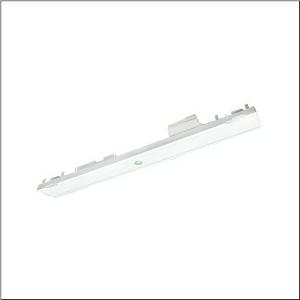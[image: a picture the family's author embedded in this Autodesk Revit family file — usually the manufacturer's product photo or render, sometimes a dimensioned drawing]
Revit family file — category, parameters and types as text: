
# Revit family: licross_r_56tl117c4x31_6d2f
name_source: partatom
category: Lighting Fixtures
units: mm (PartAtom-declared; Revit-internal decimal feet)

## family parameters
Cut with Voids When Loaded = No
Host = Face
Light Source = No
Part Type = Normal
Room Calculation Point = No
Round Connector Dimension = Use Diameter
Shared = No

## types (1)
- Licross® (1 x LED, 310 lm, 3.9 W, 4000K)
    Apparent Load = 4 VA
    CIE Flux Codes = 84 95 98 100 100
    Color Rendering = 70
    Color Temperature = 4000K
    Default Elevation = 1800 mm
    Description = Licross®, luminaire insert, of sheet steel, coil coated, white, length: 500mm, width: 59mm, height: 60mm, mounting height: 7..17m, emergency light element,LED rated luminous flux: 310lm, light colour: 740, control gear: CEAG, with plug, 6-pole, with phase selection, mains connection: 220..240V, AC/DC, 0/50..60Hz, rated input power: 3.9W, internal wiring halogen-free, for trunking rail, 9..14-core, for emergency light function, supply monitoring module CEAG, with address switch, choice between two emergency light lines via tool-free moving of contact pin prior to installation in trunking rail, primary light control with lens, of PMMA, primary optical cover: cover, of PMMA, light emission: direct distribution, primary light characteristic: symmetric,  for area, compatible with all CEAG STAR technology systems (ZB-S, DG-S (DualGuard-S), LP-STAR, AT-S+), protection rating (complete): IP40, insulation class (complete): insulation class I (protective earthing), certification: CE, UKCA, protection symbol: D if used in an environment without relevant dust loads, impact resistance: IK06, permissible ambient temperature for indoor applications: -20..+40°C, packaging unit: 1 piece
    Height = 60 mm  [stored 0.19685 ft]
    Lamp = 1 x LED
    Lamp Light Flux = 310 lm
    Lamp Power = 3.9 W
    Lamp count = 1
    Length = 500 mm  [stored 1.64042 ft]
    Luminous efficacy = 79 lm/W
    Manufacturer = Siteco
    ModVariant = No
    Model = 56TL117C4X31
    Mounting Place = Ceiling
    Mounting Type = Pendant
    Number of Poles = 1
    OnlyDefault = Yes
    Power Factor = 1
    Product Name = Licross®
    Product group = luminaire insert | ceiling pendant
    ProductGroupID = 902
    Protection Class = Protection class I
    Protection Degree = IP 40
    RLX_Detail_Level = 1
    RLX_Emergency_Light_Flux = 0 lm
    RLX_Emergency_Type = 0
    RLX_Emergency_Type_DB = No
    RlxData = <blob elided: 17853 chars, md5=111cdbb5>
    Socket = socket
    Standby Power = 0 W
    System Light Flux = 310 lm
    System Power = 4 W
    Type Comments = Product without accessories
    Type Image = l_1251804.jpg
    URL = http://relux.com
    VarID = ---
    Voltage = 0 V
    Weight = 0.00 kg
    Width = 59 mm

note: [stored X ft] marks values corroborated as IEEE doubles in the binary element streams (Revit-internal decimal feet)

## geometry (parser evidence)
native form markers: Blend x4, Sweep x12
no freeform markers — native parametric forms only
